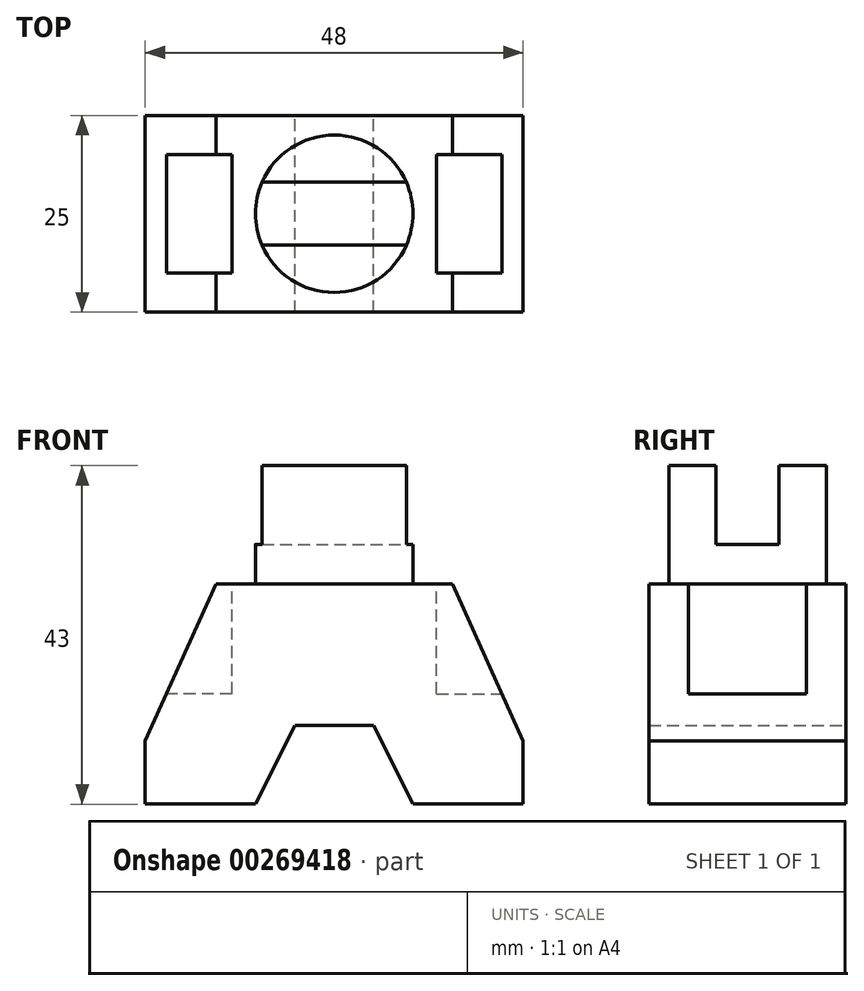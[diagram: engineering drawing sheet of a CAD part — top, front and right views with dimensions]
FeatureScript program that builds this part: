
annotation { "Feature Type Name" : "Feature", "Feature Type Description" : "" }
export const myFeature = defineFeature(function(context is Context, id is Id, definition is map)
    precondition{}
    {
        {
            var Q0;
            Q0=qCreatedBy(makeId("Front.planeOp"),FACE);
            var sketch = newSketch(context, id + "F0", { "sketchPlane" : qUnion([Q0])});
            skLineSegment(sketch, "E0", {"start": v(-21.3, -30.68) * mm, "end": v(-7.3, -30.68) * mm});
            skLineSegment(sketch, "E1", {"start": v(-7.3, -30.68) * mm, "end": v(-2.3, -20.68) * mm});
            skLineSegment(sketch, "E2", {"start": v(-2.3, -20.68) * mm, "end": v(7.7, -20.68) * mm});
            skLineSegment(sketch, "E3", {"start": v(7.7, -20.68) * mm, "end": v(12.7, -30.68) * mm});
            skLineSegment(sketch, "E4", {"start": v(12.7, -30.68) * mm, "end": v(26.7, -30.68) * mm});
            skLineSegment(sketch, "E5", {"start": v(26.7, -30.68) * mm, "end": v(26.7, -22.68) * mm});
            skLineSegment(sketch, "E6", {"start": v(26.7, -22.68) * mm, "end": v(17.7, -2.68) * mm});
            skLineSegment(sketch, "E7", {"start": v(17.7, -2.68) * mm, "end": v(-12.3, -2.68) * mm});
            skLineSegment(sketch, "E8", {"start": v(-12.3, -2.68) * mm, "end": v(-21.3, -22.68) * mm});
            skLineSegment(sketch, "E9", {"start": v(-21.3, -22.68) * mm, "end": v(-21.3, -30.68) * mm});
            skSolve(sketch);
        }
        {
            var Q0;
            Q0=makeQuery(id+"F0.imprint","IMPRINT",FACE,{"disambiguationData":[TD([[makeQuery(id+"F0.imprint","IMPRINT",EDGE,{"derivedFrom":sQuery(id+"F0.wireOp",EDGE,"E0")}),1.0]])]});
            extrude(context, id + "F1", {"entities" : qUnion([Q0]), "depth" : 25 * mm});
        }
        {
            var Q0;
            Q0=makeQuery(id+"F1.opExtrude","SWEPT_FACE",FACE,{"disambiguationData":[OSD([sQuery(id+"F0.wireOp",EDGE,"E7")])]});
            var sketch = newSketch(context, id + "F2", { "sketchPlane" : qUnion([Q0])});
            skLineSegment(sketch, "E10.bottom", {"start": v(-10.3, -5) * mm, "end": v(-19.3, -5) * mm});
            skLineSegment(sketch, "E10.top", {"start": v(-10.3, -20) * mm, "end": v(-19.3, -20) * mm});
            skLineSegment(sketch, "E10.left", {"start": v(-10.3, -5) * mm, "end": v(-10.3, -20) * mm});
            skLineSegment(sketch, "E10.right", {"start": v(-19.3, -5) * mm, "end": v(-19.3, -20) * mm});
            skSolve(sketch);
        }
        {
            var Q0;
            {var subQ0=sQuery(id+"F2.wireOp",EDGE,"E10.left");Q0=makeQuery(id+"F2.imprint","IMPRINT",FACE,{"disambiguationData":[TD([[makeQuery(id+"F2.imprint","IMPRINT",EDGE,{"derivedFrom":subQ0}),-1.0]])]});}
            var Q1;
            {var subQ0=sQuery(id+"F2.wireOp",EDGE,"E10.right");Q1=makeQuery(id+"F2.imprint","IMPRINT",FACE,{"disambiguationData":[TD([[makeQuery(id+"F2.imprint","IMPRINT",EDGE,{"derivedFrom":subQ0}),1.0]])]});}
            extrude(context, id + "F3", {"entities" : qUnion([Q0, Q1]), "operationType" : NewBodyOperationType.REMOVE, "oppositeDirection" : true, "depth" : 14 * mm});
        }
        {
            var Q0;
            Q0=makeQuery(id+"F1.opExtrude","SWEPT_FACE",FACE,{"disambiguationData":[OSD([sQuery(id+"F0.wireOp",EDGE,"E7")])]});
            var sketch = newSketch(context, id + "F4", { "sketchPlane" : qUnion([Q0])});
            skLineSegment(sketch, "E11.bottom", {"start": v(15.7, -5) * mm, "end": v(24.7, -5) * mm});
            skLineSegment(sketch, "E11.top", {"start": v(15.7, -20) * mm, "end": v(24.7, -20) * mm});
            skLineSegment(sketch, "E11.left", {"start": v(15.7, -5) * mm, "end": v(15.7, -20) * mm});
            skLineSegment(sketch, "E11.right", {"start": v(24.7, -5) * mm, "end": v(24.7, -20) * mm});
            skSolve(sketch);
        }
        {
            var Q0;
            {var subQ0=sQuery(id+"F4.wireOp",EDGE,"E11.right");Q0=makeQuery(id+"F4.imprint","IMPRINT",FACE,{"disambiguationData":[TD([[makeQuery(id+"F4.imprint","IMPRINT",EDGE,{"derivedFrom":subQ0}),-1.0]])]});}
            var Q1;
            {var subQ0=sQuery(id+"F4.wireOp",EDGE,"E11.left");Q1=makeQuery(id+"F4.imprint","IMPRINT",FACE,{"disambiguationData":[TD([[makeQuery(id+"F4.imprint","IMPRINT",EDGE,{"derivedFrom":subQ0}),1.0]])]});}
            extrude(context, id + "F5", {"entities" : qUnion([Q0, Q1]), "operationType" : NewBodyOperationType.REMOVE, "oppositeDirection" : true, "depth" : 14 * mm});
        }
        {
            var Q0;
            Q0=makeQuery(id+"F1.opExtrude","SWEPT_FACE",FACE,{"disambiguationData":[OSD([sQuery(id+"F0.wireOp",EDGE,"E7")])]});
            var sketch = newSketch(context, id + "F6", { "sketchPlane" : qUnion([Q0])});
            skCircle(sketch, "E12", {"center": v(2.7, -12.5) * mm, "radius": 10 * mm});
            skPoint(sketch, "E12.centerSnap0", {"position": v(-10.3, -12.5) * mm});
            skPoint(sketch, "E12.centerSnap1", {"position": v(2.7, -25) * mm});
            skSolve(sketch);
        }
        {
            var Q0;
            Q0=makeQuery(id+"F6.imprint","IMPRINT",FACE,{"disambiguationData":[TD([[makeQuery(id+"F6.imprint","IMPRINT",EDGE,{"derivedFrom":sQuery(id+"F6.wireOp",EDGE,"E12")}),1.0]])]});
            extrude(context, id + "F7", {"entities" : qUnion([Q0]), "operationType" : NewBodyOperationType.ADD, "depth" : 15 * mm});
        }
        {
            var Q0;
            Q0=makeQuery(id+"F7.opExtrude","CAP_FACE",FACE,{"disambiguationData":[OSD([sQuery(id+"F6.wireOp",EDGE,"E12")])],"isStart":false});
            var sketch = newSketch(context, id + "F8", { "sketchPlane" : qUnion([Q0])});
            skLineSegment(sketch, "E13", {"start": v(-6.47, -8.5) * mm, "end": v(11.86, -8.5) * mm});
            skLineSegment(sketch, "E14", {"start": v(-6.47, -16.5) * mm, "end": v(11.86, -16.5) * mm});
            skSolve(sketch);
        }
        {
            var Q0;
            {var subQ0=sQuery(id+"F8.wireOp",EDGE,"E13");Q0=makeQuery(id+"F8.imprint","IMPRINT",FACE,{"disambiguationData":[TD([[makeQuery(id+"F8.imprint","IMPRINT",EDGE,{"derivedFrom":subQ0}),-1.0]])]});}
            extrude(context, id + "F9", {"entities" : qUnion([Q0]), "operationType" : NewBodyOperationType.REMOVE, "oppositeDirection" : true, "depth" : 10 * mm});
        }
    });
